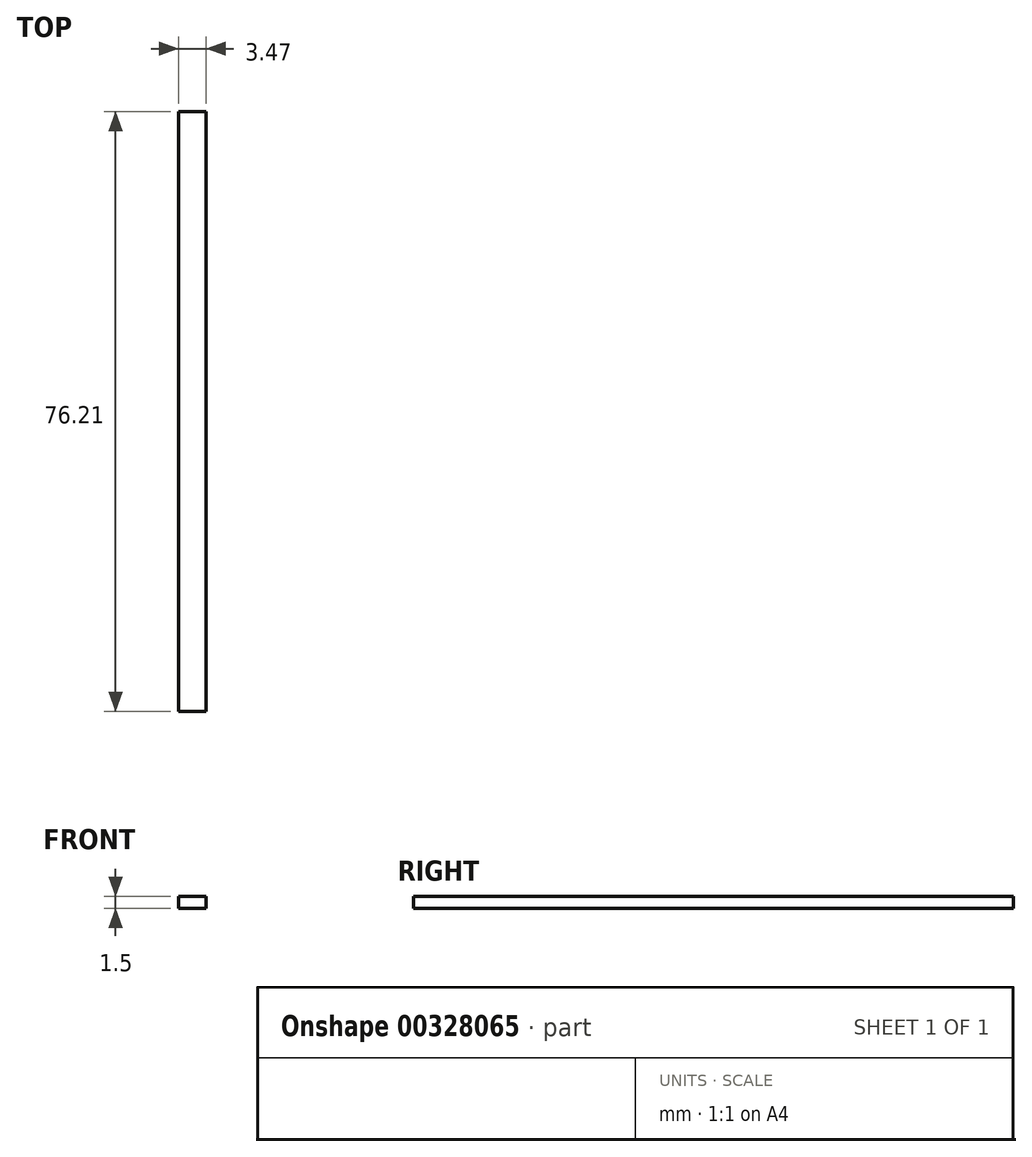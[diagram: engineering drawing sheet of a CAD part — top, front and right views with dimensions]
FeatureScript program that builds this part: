
annotation { "Feature Type Name" : "Feature", "Feature Type Description" : "" }
export const myFeature = defineFeature(function(context is Context, id is Id, definition is map)
    precondition{}
    {
        {
            var Q0;
            Q0=qCreatedBy(makeId("Top.planeOp"),FACE);
            var sketch = newSketch(context, id + "F0", { "sketchPlane" : qUnion([Q0])});
            skLineSegment(sketch, "E0", {"start": v(0, 0) * mm, "end": v(0, 76.2) * mm});
            skLineSegment(sketch, "E1", {"start": v(0, 0) * mm, "end": v(3.47, 0) * mm});
            skLineSegment(sketch, "E2", {"start": v(3.47, 0) * mm, "end": v(3.47, 76.2) * mm});
            skLineSegment(sketch, "E3", {"start": v(3.47, 76.2) * mm, "end": v(0, 76.2) * mm});
            skSolve(sketch);
        }
        {
            var Q0;
            Q0 = qSketchRegion(id + "F0", true);
            extrude(context, id + "F1", {"entities" : qUnion([Q0]), "depth" : 1.5 * mm});
        }
    });
